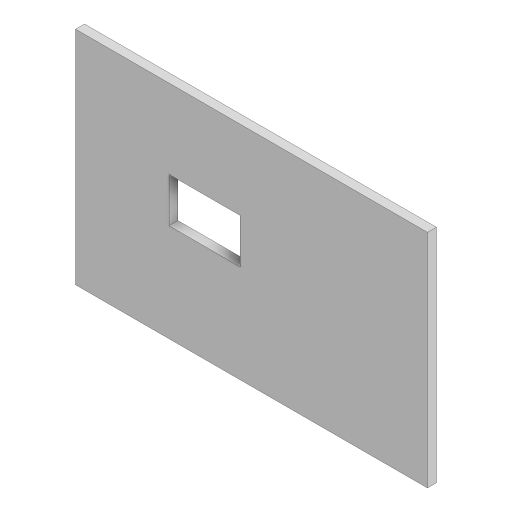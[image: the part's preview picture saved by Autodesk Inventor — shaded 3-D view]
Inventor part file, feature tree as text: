
AUTODESK INVENTOR PART (.ipt)
format: ipt  version: 2024.1 (Build 281209000, 209)  size: 117,248 bytes
history: native  units: in
note: dims shown in document units (in); Inventor stores cm internally (conversion verified against a paired STEP export)
features: extrude x1, sketch x1
ambient origin geometry x8: Origin, YZ Plane, XZ Plane, XY Plane, X Axis, Y Axis, Z Axis, Center Point
bodies: Solid1 (feature_tree)
feature tree (2):
  extrude  "Extrusion1"  Depth=1.9685in
  sketch  "Sketch1"  dims[d0=3.1496in d1=1.9685in d2=0.3937in d3=0.0in d4=4.1339in d5=4.3307in]
